# Revit family: BA-04
name_source: partatom
category: Устройства связи
revit_build: Autodesk Revit 2016 (Build: 20160314_0715(x64)
units: mm (PartAtom-declared; Revit-internal decimal feet)

## family parameters
Всегда вертикально = Нет
На основе рабочей плоскости = Да
Общий = Да
При загрузке вырезать с полостями = Нет
Размер круглого соединителя = Использовать диаметр
Сохранять ориентацию аннотаций = Нет
Тип детали = Нормальный
Точка расчета площади = Нет

## types (2) — shared parameters
ADSK_URL документации изделия = https://wiki.bas-ip.com
ADSK_URL страницы изделия = https://www.bas-ip.ru
ADSK_Версия Revit = Revit 2016
ADSK_Единица измерения = шт
ADSK_Завод-изготовитель = BAS-IP
ADSK_Классификация нагрузок = Вызывная панель
ADSK_Количество фаз = 1
ADSK_Коэффициент мощности = 0.9
ADSK_Напряжение = 12 В
ADSK_Номинальная мощность = 7 Вт
ADSK_Полная мощность = 7 В·А
ADSK_Размер_Длина = 155 мм
ADSK_Размер_Толщина = 50 мм
ADSK_Размер_Ширина = 270 мм
BIM library = https://bimlib.ru
URL = https://www.bas-ip.ru
Аутентификация = Отдельный пароль на настройки, WEB–интерфейс
Выходное видео = D1 (704х576), H.264 Main Profile, BaseLine Profile
Группа модели = Вызывная панель
Дисплей = Нет
Дополнительно = SIP P2P, Встроенное реле
Изготовитель = BAS-IP
Изображение = SHV_Изображение_BA-04
Изображение типоразмера = <Нет>
Интеграция со СКУД = Выход WIEGAND-26
Интерфейс = WEB-интерфейс
Камера = 1/3”, регулировка направления камеры
Класс степени защиты = IP65
Кнопки быстрого вызова = Кнопка вызова консьержа
Количество мелодий вызова = 4 полифонические мелодии
Контроль доступа = Считыватель беcконтактных карт EM-Marin (BA-04E), Mifare (BA-04M)
Корпус = Металлический
Материал корпуса = Серебро
Минимальная освещенность = 0,01 LuX
Ночная подсветка = 6 светодиодов
Описание = BA-04E SILVER / BA-04M SILVER – это 4-х абонентская панель, которая прекрасно объединяет в себе доступность, красивый и стильный дизайн, а также прекрасные технические характеристики.
Открытие замка = С монитора, по карте, из приложения BAS-IP Intercom
Питание = +12 В
Потребление питания = 6,5 Вт, в режиме ожидания – 2,5 Вт
Размер под установку = 150х250х60 мм
Размер самой панели = 155х270х50 мм
Разрешение камеры = 800 ТВл
Режим разговора = Двухсторонний
Температурный режим = -40 ... +65 °С
Тип клавиатуры = Механические кнопки с подсветкой
Тип панели = Многоквартирная
Тип установки = Врезная, накладная с BR-BA
Угол обзора = По горизонтали 78°, по вертикали 56°
Цветовое решение = Серебристо-серый
zero-valued in all types: Отметка по умолчанию

## per-type parameters (varying)
| type | ADSK_Марка | ADSK_Наименование | ADSK_Наименование краткое |
| BA-04E SILVER | BA-04E | ВЫЗЫВНАЯ ПАНЕЛЬ BA-04E | BA-04E |
| BA-04M SILVER | BA-04M | ВЫЗЫВНАЯ ПАНЕЛЬ BA-04M | BA-04M |
